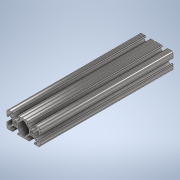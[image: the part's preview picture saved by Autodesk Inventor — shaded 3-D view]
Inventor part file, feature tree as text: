
AUTODESK INVENTOR PART (.ipt)
format: ipt  version: 2020 (Build 240168000, 168)  size: 343,040 bytes
history: native  units: in
note: dims shown in document units (in); Inventor stores cm internally (conversion verified against a paired STEP export)
features: sketch x2, extrude x1
ambient origin geometry x8: Origin, YZ Plane, XZ Plane, XY Plane, X Axis, Y Axis, Z Axis, Center Point
bodies: Solid1 (feature_tree)
feature tree (3):
  extrude  "Extrusion1"  [1 undecoded]
  sketch  "Sketch2"
  sketch  "Sketch1"  dims[d0=8.0in d1=0.0in]
note: 1 required parameter value undecoded (feature->parameter linkage not recoverable at this tier; creation-order binding heuristic only, values carry confidence <= 0.55)
